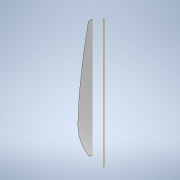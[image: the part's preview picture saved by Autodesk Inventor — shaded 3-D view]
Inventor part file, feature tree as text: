
AUTODESK INVENTOR PART (.ipt)
format: ipt  version: 2022 (Build 260153000, 153)  size: 939,008 bytes
history: native  units: mm
features: sketch x4, plane x1, sweep x1
ambient origin geometry x8: Origin, YZ Plane, XZ Plane, XY Plane, X Axis, Y Axis, Z Axis, Center Point
bodies: Body1 (feature_tree)
feature tree (6):
  sketch  "Sketch1"  dims[d0=330.0mm d3=30.0mm]
  sketch  "Sketch2"  dims[d12=0.0mm d13=0.0mm]
  plane  "Work Plane1"
  sketch  "3D Sketch1"
  sketch  "Sketch4"
  sweep  "Sweep6"
